# Revit family: Grohe_PlumbingFixtures_WC_Cistern_38661000
name_source: partatom
category: Plumbing Fixtures
revit_build: Autodesk Revit 2017 (Build: 20161117_1200(x64)
units: mm (PartAtom-declared; Revit-internal decimal feet)

## family parameters
Cut with Voids When Loaded = Yes
Host = Face
OmniClass Number = 23.45.05.21
OmniClass Title = Plumbing Fixtures - Sanitary Disposal Units
Part Type = Normal
Room Calculation Point = No
Round Connector Dimension = Use Diameter
Shared = No

## types (1)
- 38661000
    Assembly Code = D2010
    AssetType = Fixed
    BIMObjectName = Grohe_PlumbingFixtures_WC_Cistern_38661000
    CW Connection = No
    ClassificationName = Uniclass2015
    ClassificationValue = Pr_40_20_93_89
    Color = White
    Default Elevation = 0 mm  [stored 0 ft]
    Description = WC concealed cistern - 38661000
    DocumentationTechnical = https://www.bimstore.co
    DurationUnit = Years
    ExpectedLife = 0
    Features = WC concealed cistern - 38661000
    Finish = Plastic
    HW Connection = No
    IfcExportAs = IfcFlowTerminalType
    IfcExportType = IfcSanitaryTerminalTypeEnum.CISTERN
    Keynote = N13
    Manufacturer = Grohe
    ManufacturerName = Grohe
    Material = Plastic
    Model = WC concealed cistern
    ModelNumber = 38661000
    ModelReference = WC concealed cistern
    NBSDescription = Grohe - WC cisterns
    NBSObjectName = WC cisterns
    NBSReference = 45-35-70/383
    NominalDepth = 118 mm
    NominalHeight = 519 mm
    NominalLength = 467 mm  [stored 1.53215 ft]
    ProductionYear = 2019
    R = 95 mm
    Shape = Rectangle
    Type Comments = 38661000
    TypeName = WC concealed cistern
    URL = https://www.grohe.co.uk
    Vent Connection = No
    WarrantyDurationLabor = 0
    WarrantyDurationParts = 0
    WarrantyDurationUnit = Years
    Waste Connection = Yes
    _BSBibleVersion = 16
    _BimSpecGuid = 0
    _CurrentRevision = 1
    _DistributedBy = www.bimstore.co.uk

note: [stored X ft] marks values corroborated as IEEE doubles in the binary element streams (Revit-internal decimal feet)

## geometry (parser evidence)
native form markers: Sweep x2
no freeform markers — native parametric forms only
